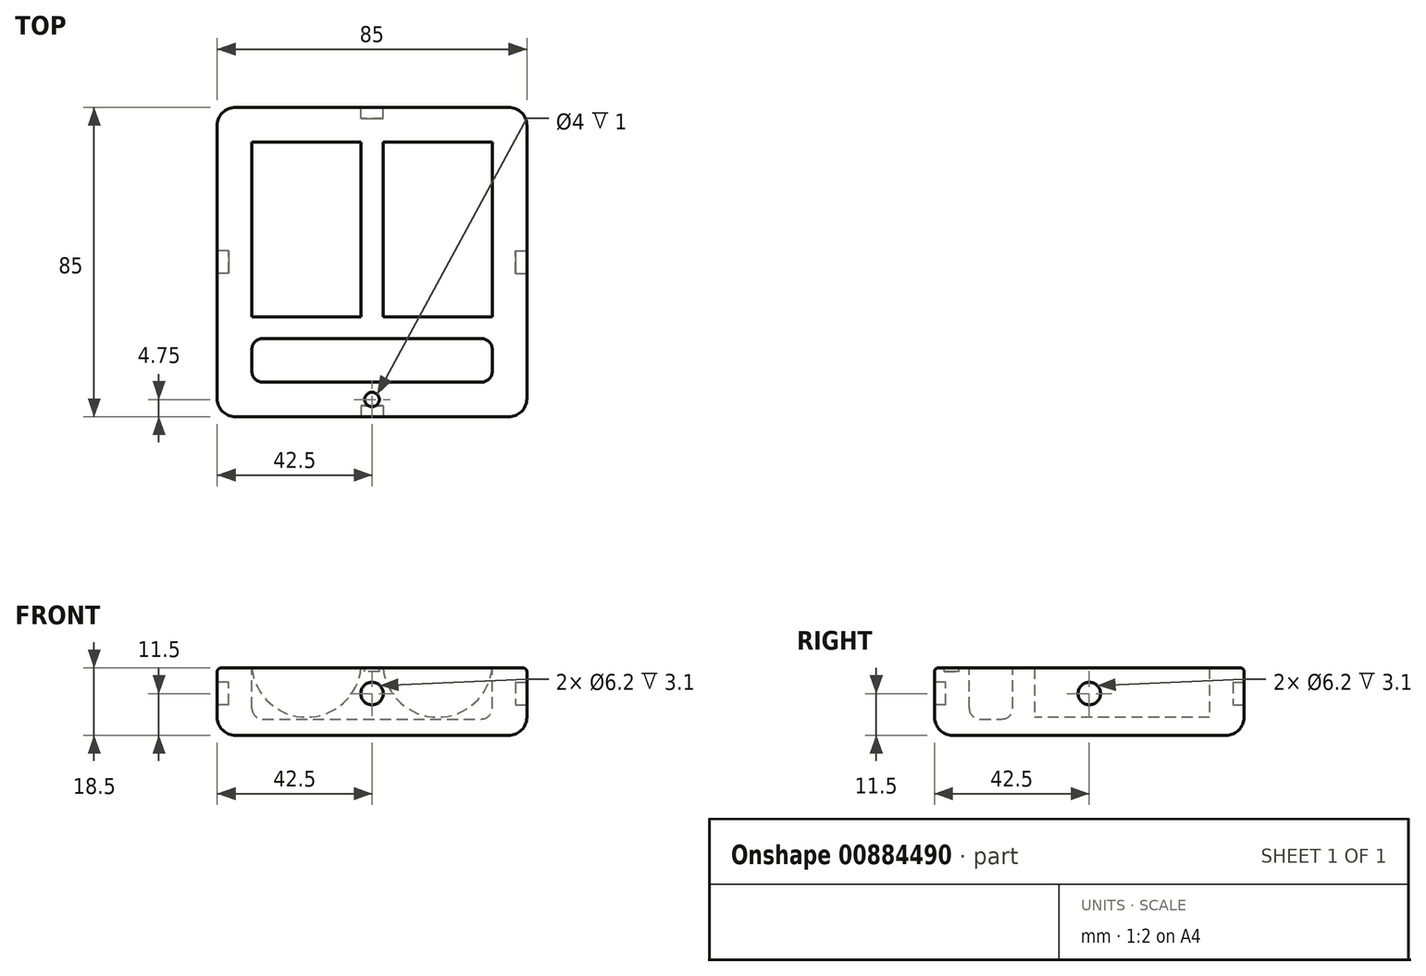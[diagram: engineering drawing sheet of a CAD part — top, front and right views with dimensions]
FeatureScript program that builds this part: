
annotation { "Feature Type Name" : "Feature", "Feature Type Description" : "" }
export const myFeature = defineFeature(function(context is Context, id is Id, definition is map)
    precondition{}
    {
        {
            var Q0;
            Q0=qCreatedBy(makeId("Top.planeOp"),FACE);
            var sketch = newSketch(context, id + "F0", { "sketchPlane" : qUnion([Q0])});
            skLineSegment(sketch, "E0.bottom", {"start": v(-42.5, 42.5) * mm, "end": v(42.5, 42.5) * mm});
            skLineSegment(sketch, "E0.top", {"start": v(-42.5, -42.5) * mm, "end": v(42.5, -42.5) * mm});
            skLineSegment(sketch, "E0.left", {"start": v(-42.5, 42.5) * mm, "end": v(-42.5, -42.5) * mm});
            skLineSegment(sketch, "E0.right", {"start": v(42.5, 42.5) * mm, "end": v(42.5, -42.5) * mm});
            skLineSegment(sketch, "E1.bottom", {"start": v(-30, 33) * mm, "end": v(30, 33) * mm});
            skLineSegment(sketch, "E1.top", {"start": v(-30, 21) * mm, "end": v(30, 21) * mm});
            skLineSegment(sketch, "E1.left", {"start": v(-33, 30) * mm, "end": v(-33, 24) * mm});
            skLineSegment(sketch, "E1.right", {"start": v(33, 30) * mm, "end": v(33, 24) * mm});
            skLineSegment(sketch, "E2.direction1", {"start": v(-33, 21) * mm, "end": v(-8.24, 21) * mm, "construction": true});
            skPoint(sketch, "E3.visualSharp", {"position": v(-33, 33) * mm});
            skArc(sketch, "E3.filletArc", {"start": v(-30, 33) * mm, "mid": v(-32.12, 32.12) * mm, "end": v(-33, 30) * mm});
            skPoint(sketch, "E4.visualSharp", {"position": v(33, 33) * mm});
            skArc(sketch, "E4.filletArc", {"start": v(33, 30) * mm, "mid": v(32.12, 32.12) * mm, "end": v(30, 33) * mm});
            skPoint(sketch, "E5.visualSharp", {"position": v(33, 21) * mm});
            skArc(sketch, "E5.filletArc", {"start": v(30, 21) * mm, "mid": v(32.12, 21.88) * mm, "end": v(33, 24) * mm});
            skPoint(sketch, "E6.visualSharp", {"position": v(-33, 21) * mm});
            skArc(sketch, "E6.filletArc", {"start": v(-33, 24) * mm, "mid": v(-32.12, 21.88) * mm, "end": v(-30, 21) * mm});
            skLineSegment(sketch, "E7.direction1", {"start": v(-33, 21) * mm, "end": v(-6.5, 21) * mm, "construction": true});
            skLineSegment(sketch, "E8", {"start": v(-42.5, 0) * mm, "end": v(42.5, 0) * mm, "construction": true});
            skLineSegment(sketch, "E9", {"start": v(0, -42.5) * mm, "end": v(0, 42.5) * mm, "construction": true});
            skCircle(sketch, "E10", {"center": v(0, 37.75) * mm, "radius": 2 * mm});
            skSolve(sketch);
        }
        {
            assignVariable(context, id + "F1", {"name" : "h", "anyValue" : 18.5});
        }
        {
            assignVariable(context, id + "F2", {"name" : "d", "anyValue" : 14});
        }
        {
            var Q0;
            Q0=makeQuery(id+"F0.imprint","IMPRINT",FACE,{"disambiguationData":[TD([[makeQuery(id+"F0.imprint","IMPRINT",EDGE,{"derivedFrom":sQuery(id+"F0.wireOp",EDGE,"E1.bottom")}),-1.0]])]});
            var Q1;
            Q1=makeQuery(id+"F0.imprint","IMPRINT",FACE,{"disambiguationData":[TD([[makeQuery(id+"F0.imprint","IMPRINT",EDGE,{"derivedFrom":sQuery(id+"F0.wireOp",EDGE,"E0.bottom")}),-1.0]])]});
            var Q2;
            Q2=makeQuery(id+"F0.imprint","IMPRINT",FACE,{"disambiguationData":[TD([[makeQuery(id+"F0.imprint","IMPRINT",EDGE,{"derivedFrom":sQuery(id+"F0.wireOp",EDGE,"E2.0.2.0")}),1.0]])]});
            var Q3;
            Q3=makeQuery(id+"F0.imprint","IMPRINT",FACE,{"disambiguationData":[TD([[makeQuery(id+"F0.imprint","IMPRINT",EDGE,{"derivedFrom":sQuery(id+"F0.wireOp",EDGE,"E2.0.3.0")}),1.0]])]});
            var Q4;
            Q4=makeQuery(id+"F0.imprint","IMPRINT",FACE,{"disambiguationData":[TD([[makeQuery(id+"F0.imprint","IMPRINT",EDGE,{"derivedFrom":sQuery(id+"F0.wireOp",EDGE,"E2.0.1.0")}),1.0]])]});
            var Q5;
            Q5=makeQuery(id+"F0.imprint","IMPRINT",FACE,{"disambiguationData":[TD([[makeQuery(id+"F0.imprint","IMPRINT",EDGE,{"derivedFrom":sQuery(id+"F0.wireOp",EDGE,"E7.0.1.2")}),1.0]])]});
            var Q6;
            Q6=makeQuery(id+"F0.imprint","IMPRINT",FACE,{"disambiguationData":[TD([[makeQuery(id+"F0.imprint","IMPRINT",EDGE,{"derivedFrom":sQuery(id+"F0.wireOp",EDGE,"E7.0.2.2")}),1.0]])]});
            var Q7;
            Q7=makeQuery(id+"F0.imprint","IMPRINT",FACE,{"disambiguationData":[TD([[makeQuery(id+"F0.imprint","IMPRINT",EDGE,{"derivedFrom":sQuery(id+"F0.wireOp",EDGE,"E7.0.3.2")}),1.0]])]});
            var Q8;
            Q8=makeQuery(id+"F0.imprint","IMPRINT",FACE,{"disambiguationData":[TD([[makeQuery(id+"F0.imprint","IMPRINT",EDGE,{"derivedFrom":sQuery(id+"F0.wireOp",EDGE,"46291ff4-7ef9-4f3a-836c-92f4481a90b5.bottom")}),-1.0]])]});
            var Q9;
            Q9=makeQuery(id+"F0.imprint","IMPRINT",FACE,{"disambiguationData":[TD([[makeQuery(id+"F0.imprint","IMPRINT",EDGE,{"derivedFrom":sQuery(id+"F0.wireOp",EDGE,"E10")}),1.0]])]});
            extrude(context, id + "F3", {"entities" : qUnion([Q0, Q1, Q2, Q3, Q4, Q5, Q6, Q7, Q8, Q9]), "depth" : (getVariable(context, 'h')) * mm, "offsetDistance" : 25 * mm});
        }
        {
            var Q0;
            Q0=makeQuery(id+"F0.imprint","IMPRINT",FACE,{"disambiguationData":[TD([[makeQuery(id+"F0.imprint","IMPRINT",EDGE,{"derivedFrom":sQuery(id+"F0.wireOp",EDGE,"E1.bottom")}),-1.0]])]});
            var Q1;
            Q1=makeQuery(id+"F0.imprint","IMPRINT",FACE,{"disambiguationData":[TD([[makeQuery(id+"F0.imprint","IMPRINT",EDGE,{"derivedFrom":sQuery(id+"F0.wireOp",EDGE,"E2.0.1.0")}),1.0]])]});
            var Q2;
            Q2=makeQuery(id+"F0.imprint","IMPRINT",FACE,{"disambiguationData":[TD([[makeQuery(id+"F0.imprint","IMPRINT",EDGE,{"derivedFrom":sQuery(id+"F0.wireOp",EDGE,"E2.0.2.0")}),1.0]])]});
            var Q3;
            Q3=makeQuery(id+"F0.imprint","IMPRINT",FACE,{"disambiguationData":[TD([[makeQuery(id+"F0.imprint","IMPRINT",EDGE,{"derivedFrom":sQuery(id+"F0.wireOp",EDGE,"E2.0.3.0")}),1.0]])]});
            var Q4;
            Q4=makeQuery(id+"F0.imprint","IMPRINT",FACE,{"disambiguationData":[TD([[makeQuery(id+"F0.imprint","IMPRINT",EDGE,{"derivedFrom":sQuery(id+"F0.wireOp",EDGE,"E7.0.1.2")}),1.0]])]});
            var Q5;
            Q5=makeQuery(id+"F0.imprint","IMPRINT",FACE,{"disambiguationData":[TD([[makeQuery(id+"F0.imprint","IMPRINT",EDGE,{"derivedFrom":sQuery(id+"F0.wireOp",EDGE,"E7.0.2.2")}),1.0]])]});
            var Q6;
            Q6=makeQuery(id+"F0.imprint","IMPRINT",FACE,{"disambiguationData":[TD([[makeQuery(id+"F0.imprint","IMPRINT",EDGE,{"derivedFrom":sQuery(id+"F0.wireOp",EDGE,"E7.0.3.2")}),1.0]])]});
            var Q7;
            Q7=makeQuery(id+"F0.imprint","IMPRINT",FACE,{"disambiguationData":[TD([[makeQuery(id+"F0.imprint","IMPRINT",EDGE,{"derivedFrom":sQuery(id+"F0.wireOp",EDGE,"46291ff4-7ef9-4f3a-836c-92f4481a90b5.bottom")}),-1.0]])]});
            extrude(context, id + "F4", {"entities" : qUnion([Q0, Q1, Q2, Q3, Q4, Q5, Q6, Q7]), "operationType" : NewBodyOperationType.REMOVE, "depth" : (getVariable(context, 'd')) * mm, "offsetDistance" : 25 * mm});
        }
        {
            var Q0;
            Q0=makeQuery(id+"F3.opExtrude","CAP_FACE",FACE,{"disambiguationData":[OSD([sQuery(id+"F0.wireOp",EDGE,"E0.bottom"),sQuery(id+"F0.wireOp",EDGE,"E0.top"),sQuery(id+"F0.wireOp",EDGE,"E0.left"),sQuery(id+"F0.wireOp",EDGE,"E0.right")])],"isStart":false});
            var Q1;
            Q1=makeQuery(id+"F3.opExtrude","SWEPT_EDGE",EDGE,{"disambiguationData":[OSD([sQuery(id+"F0.wireOp",EDGE,"E0.bottom"),sQuery(id+"F0.wireOp",EDGE,"E0.right")])]});
            var Q2;
            Q2=makeQuery(id+"F3.opExtrude","SWEPT_EDGE",EDGE,{"disambiguationData":[OSD([sQuery(id+"F0.wireOp",EDGE,"E0.bottom"),sQuery(id+"F0.wireOp",EDGE,"E0.left")])]});
            var Q3;
            Q3=makeQuery(id+"F3.opExtrude","SWEPT_EDGE",EDGE,{"disambiguationData":[OSD([sQuery(id+"F0.wireOp",EDGE,"E0.top"),sQuery(id+"F0.wireOp",EDGE,"E0.left")])]});
            var Q4;
            Q4=makeQuery(id+"F3.opExtrude","SWEPT_EDGE",EDGE,{"disambiguationData":[OSD([sQuery(id+"F0.wireOp",EDGE,"E0.top"),sQuery(id+"F0.wireOp",EDGE,"E0.right")])]});
            fillet(context, id + "F5", {"entities" : qUnion([Q0, Q1, Q2, Q3, Q4]), "radius" : 5 * mm, "tangentPropagation" : true, "allowEdgeOverflow" : false});
        }
        {
            var Q0;
            Q0=makeQuery(id+"F4.boolean.opBoolean","COPY",FACE,{"derivedFrom":makeQuery(id+"F4.opExtrude","CAP_FACE",FACE,{"disambiguationData":[OSD([sQuery(id+"F0.wireOp",EDGE,"E1.bottom"),sQuery(id+"F0.wireOp",EDGE,"E1.top"),sQuery(id+"F0.wireOp",EDGE,"E1.left"),sQuery(id+"F0.wireOp",EDGE,"E1.right"),sQuery(id+"F0.wireOp",EDGE,"E3.filletArc"),sQuery(id+"F0.wireOp",EDGE,"E4.filletArc"),sQuery(id+"F0.wireOp",EDGE,"E5.filletArc"),sQuery(id+"F0.wireOp",EDGE,"E6.filletArc")])],"isStart":false})});
            var Q1;
            Q1=makeQuery(id+"F4.boolean.opBoolean","COPY",FACE,{"derivedFrom":makeQuery(id+"F4.opExtrude","CAP_FACE",FACE,{"disambiguationData":[OSD([sQuery(id+"F0.wireOp",EDGE,"E7.0.1.2"),sQuery(id+"F0.wireOp",EDGE,"E7.0.1.4"),sQuery(id+"F0.wireOp",EDGE,"E7.0.1.5"),sQuery(id+"F0.wireOp",EDGE,"E7.0.1.6"),sQuery(id+"F0.wireOp",EDGE,"E7.0.1.7"),sQuery(id+"F0.wireOp",EDGE,"E7.0.1.9"),sQuery(id+"F0.wireOp",EDGE,"E7.0.1.11"),sQuery(id+"F0.wireOp",EDGE,"E7.0.1.12")])],"isStart":false})});
            var Q2;
            Q2=makeQuery(id+"F4.boolean.opBoolean","COPY",FACE,{"derivedFrom":makeQuery(id+"F4.opExtrude","CAP_FACE",FACE,{"disambiguationData":[OSD([sQuery(id+"F0.wireOp",EDGE,"E7.0.2.2"),sQuery(id+"F0.wireOp",EDGE,"E7.0.2.4"),sQuery(id+"F0.wireOp",EDGE,"E7.0.2.5"),sQuery(id+"F0.wireOp",EDGE,"E7.0.2.6"),sQuery(id+"F0.wireOp",EDGE,"E7.0.2.7"),sQuery(id+"F0.wireOp",EDGE,"E7.0.2.9"),sQuery(id+"F0.wireOp",EDGE,"E7.0.2.11"),sQuery(id+"F0.wireOp",EDGE,"E7.0.2.12")])],"isStart":false})});
            var Q3;
            Q3=makeQuery(id+"F4.boolean.opBoolean","COPY",FACE,{"derivedFrom":makeQuery(id+"F4.opExtrude","CAP_FACE",FACE,{"disambiguationData":[OSD([sQuery(id+"F0.wireOp",EDGE,"E7.0.3.2"),sQuery(id+"F0.wireOp",EDGE,"E7.0.3.4"),sQuery(id+"F0.wireOp",EDGE,"E7.0.3.5"),sQuery(id+"F0.wireOp",EDGE,"E7.0.3.6"),sQuery(id+"F0.wireOp",EDGE,"E7.0.3.7"),sQuery(id+"F0.wireOp",EDGE,"E7.0.3.9"),sQuery(id+"F0.wireOp",EDGE,"E7.0.3.11"),sQuery(id+"F0.wireOp",EDGE,"E7.0.3.12")])],"isStart":false})});
            var Q4;
            Q4=makeQuery(id+"F4.boolean.opBoolean","COPY",FACE,{"derivedFrom":makeQuery(id+"F4.opExtrude","CAP_FACE",FACE,{"disambiguationData":[OSD([sQuery(id+"F0.wireOp",EDGE,"46291ff4-7ef9-4f3a-836c-92f4481a90b5.bottom"),sQuery(id+"F0.wireOp",EDGE,"46291ff4-7ef9-4f3a-836c-92f4481a90b5.top"),sQuery(id+"F0.wireOp",EDGE,"46291ff4-7ef9-4f3a-836c-92f4481a90b5.left"),sQuery(id+"F0.wireOp",EDGE,"46291ff4-7ef9-4f3a-836c-92f4481a90b5.right"),sQuery(id+"F0.wireOp",EDGE,"f9652c3b-33d4-4875-8296-8c731cea0ff2.filletArc"),sQuery(id+"F0.wireOp",EDGE,"bc3a633f-a680-41aa-ad19-7ac7e5a684a1.filletArc"),sQuery(id+"F0.wireOp",EDGE,"cd018c40-e85b-49f8-971f-61b861827422.filletArc"),sQuery(id+"F0.wireOp",EDGE,"71912b40-0116-4324-a46e-baf74d7a231e.filletArc")])],"isStart":false})});
            fillet(context, id + "F6", {"entities" : qUnion([Q0, Q1, Q2, Q3, Q4]), "radius" : 3 * mm, "tangentPropagation" : true, "allowEdgeOverflow" : false});
        }
        {
            var Q0;
            Q0=makeQuery(id+"F3.opExtrude","SWEPT_FACE",FACE,{"disambiguationData":[OSD([sQuery(id+"F0.wireOp",EDGE,"E0.top")])]});
            var sketch = newSketch(context, id + "F7", { "sketchPlane" : qUnion([Q0])});
            skCircle(sketch, "E11", {"center": v(0, 7) * mm, "radius": 3.1 * mm});
            skSolve(sketch);
        }
        {
            var Q0;
            Q0=makeQuery(id+"F7.imprint","IMPRINT",FACE,{"disambiguationData":[TD([[makeQuery(id+"F7.imprint","IMPRINT",EDGE,{"derivedFrom":sQuery(id+"F7.wireOp",EDGE,"E11")}),1.0]])]});
            extrude(context, id + "F8", {"entities" : qUnion([Q0]), "operationType" : NewBodyOperationType.REMOVE, "oppositeDirection" : true, "depth" : 3.1 * mm, "offsetDistance" : 25 * mm});
        }
        {
            var Q0;
            Q0=makeQuery(id+"F3.opExtrude","SWEPT_FACE",FACE,{"disambiguationData":[OSD([sQuery(id+"F0.wireOp",EDGE,"E0.bottom")])]});
            var sketch = newSketch(context, id + "F9", { "sketchPlane" : qUnion([Q0])});
            skCircle(sketch, "E12", {"center": v(0, 7) * mm, "radius": 3.1 * mm});
            skSolve(sketch);
        }
        {
            var Q0;
            Q0=makeQuery(id+"F9.imprint","IMPRINT",FACE,{"disambiguationData":[TD([[makeQuery(id+"F9.imprint","IMPRINT",EDGE,{"derivedFrom":sQuery(id+"F9.wireOp",EDGE,"E12")}),1.0]])]});
            extrude(context, id + "F10", {"entities" : qUnion([Q0]), "operationType" : NewBodyOperationType.REMOVE, "oppositeDirection" : true, "depth" : 3.1 * mm, "offsetDistance" : 25 * mm});
        }
        {
            var Q0;
            Q0=makeQuery(id+"F3.opExtrude","SWEPT_FACE",FACE,{"disambiguationData":[OSD([sQuery(id+"F0.wireOp",EDGE,"E0.left")])]});
            var sketch = newSketch(context, id + "F11", { "sketchPlane" : qUnion([Q0])});
            skCircle(sketch, "E13", {"center": v(0, 7) * mm, "radius": 3.1 * mm});
            skSolve(sketch);
        }
        {
            var Q0;
            Q0=makeQuery(id+"F11.imprint","IMPRINT",FACE,{"disambiguationData":[TD([[makeQuery(id+"F11.imprint","IMPRINT",EDGE,{"derivedFrom":sQuery(id+"F11.wireOp",EDGE,"E13")}),1.0]])]});
            extrude(context, id + "F12", {"entities" : qUnion([Q0]), "operationType" : NewBodyOperationType.REMOVE, "oppositeDirection" : true, "depth" : 3.1 * mm, "offsetDistance" : 25 * mm});
        }
        {
            var Q0;
            Q0=makeQuery(id+"F3.opExtrude","SWEPT_FACE",FACE,{"disambiguationData":[OSD([sQuery(id+"F0.wireOp",EDGE,"E0.right")])]});
            var sketch = newSketch(context, id + "F13", { "sketchPlane" : qUnion([Q0])});
            skCircle(sketch, "E14", {"center": v(0, 7) * mm, "radius": 3.1 * mm});
            skSolve(sketch);
        }
        {
            var Q0;
            Q0=makeQuery(id+"F13.imprint","IMPRINT",FACE,{"disambiguationData":[TD([[makeQuery(id+"F13.imprint","IMPRINT",EDGE,{"derivedFrom":sQuery(id+"F13.wireOp",EDGE,"E14")}),1.0]])]});
            extrude(context, id + "F14", {"entities" : qUnion([Q0]), "operationType" : NewBodyOperationType.REMOVE, "oppositeDirection" : true, "depth" : 3.1 * mm, "offsetDistance" : 25 * mm});
        }
        {
            var Q0;
            Q0=makeQuery(id+"F0.imprint","IMPRINT",FACE,{"disambiguationData":[TD([[makeQuery(id+"F0.imprint","IMPRINT",EDGE,{"derivedFrom":sQuery(id+"F0.wireOp",EDGE,"E10")}),1.0]])]});
            extrude(context, id + "F15", {"entities" : qUnion([Q0]), "operationType" : NewBodyOperationType.REMOVE, "depth" : 1 * mm, "offsetDistance" : 25 * mm});
        }
        {
            var Q0;
            Q0=makeQuery(id+"F3.opExtrude","SWEPT_FACE",FACE,{"disambiguationData":[OSD([sQuery(id+"F0.wireOp",EDGE,"E0.bottom")])]});
            cPlane(context, id + "F16", {"entities" : qUnion([Q0]), "cplaneType" : CPlaneType.OFFSET, "offset" : 27.5 * mm, "oppositeDirection" : true, "width" : 150 * mm, "height" : 150 * mm});
        }
        {
            var Q0;
            Q0=qCreatedBy(id+"F16.planeOp",FACE);
            var sketch = newSketch(context, id + "F17", { "sketchPlane" : qUnion([Q0])});
            skArc(sketch, "E15", {"start": v(-3, 0) * mm, "mid": v(-18, 13.5) * mm, "end": v(-33, 0) * mm});
            skLineSegment(sketch, "E16", {"start": v(-3, 0) * mm, "end": v(-3, 13.5) * mm, "construction": true});
            skLineSegment(sketch, "E17", {"start": v(-33, 13.5) * mm, "end": v(-33, 0) * mm, "construction": true});
            skLineSegment(sketch, "E18", {"start": v(-33, 13.5) * mm, "end": v(-3, 13.5) * mm, "construction": true});
            skPoint(sketch, "E18.endSnap0", {"position": v(-3, 16.26) * mm});
            skLineSegment(sketch, "E19.trimOffspring", {"start": v(-3, 16.26) * mm, "end": v(-3, 35.2) * mm, "construction": true});
            skLineSegment(sketch, "E20", {"start": v(-33, 0) * mm, "end": v(-3, 0) * mm});
            skPoint(sketch, "E21.orphan", {"position": v(-47.15, 0) * mm});
            skPoint(sketch, "E22.orphan", {"position": v(-3, -2.69) * mm});
            skLineSegment(sketch, "E23.MirrorCS", {"start": v(33, 0) * mm, "end": v(3, 0) * mm});
            skArc(sketch, "E24.MirrorCS", {"start": v(3, 0) * mm, "mid": v(18, 13.5) * mm, "end": v(33, 0) * mm});
            skSolve(sketch);
        }
        {
            var Q0;
            Q0=makeQuery(id+"F17.imprint","IMPRINT",FACE,{"disambiguationData":[TD([[makeQuery(id+"F17.imprint","IMPRINT",EDGE,{"derivedFrom":sQuery(id+"F17.wireOp",EDGE,"E15")}),1.0]])]});
            var Q1;
            Q1=makeQuery(id+"F17.imprint","IMPRINT",FACE,{"disambiguationData":[TD([[makeQuery(id+"F17.imprint","IMPRINT",EDGE,{"derivedFrom":sQuery(id+"F17.wireOp",EDGE,"E23.MirrorCS")}),-1.0]])]});
            extrude(context, id + "F18", {"entities" : qUnion([Q0, Q1]), "operationType" : NewBodyOperationType.REMOVE, "oppositeDirection" : true, "depth" : 48 * mm, "offsetDistance" : 25 * mm});
        }
        {
            var Q0;
            Q0=makeQuery(id+"F3.opExtrude","CAP_EDGE",EDGE,{"disambiguationData":[OSD([sQuery(id+"F0.wireOp",EDGE,"E0.left")])],"isStart":true});
            var Q1;
            {var subQ0=sQuery(id+"F17.wireOp",EDGE,"E24.MirrorCS");var subQ1=sQuery(id+"F17.wireOp",EDGE,"E23.MirrorCS");Q1=makeQuery(id+"F18.boolean.opBoolean","COPY",EDGE,{"derivedFrom":makeQuery(id+"F18.opExtrude","SWEPT_EDGE",EDGE,{"disambiguationData":[OSD([subQ1,subQ0]),TDD([makeQuery(id+"F17.imprint","INTERSECT",VERTEX,{"disambiguationData":[OD(0.0)],"derivedFrom":[subQ1,subQ0]})])]})});}
            var Q2;
            Q2=makeQuery(id+"F18.boolean.opBoolean","COPY",EDGE,{"derivedFrom":makeQuery(id+"F18.opExtrude","CAP_EDGE",EDGE,{"disambiguationData":[OSD([sQuery(id+"F17.wireOp",EDGE,"E23.MirrorCS")])],"isStart":true})});
            var Q3;
            {var subQ0=sQuery(id+"F17.wireOp",EDGE,"E24.MirrorCS");var subQ1=sQuery(id+"F17.wireOp",EDGE,"E23.MirrorCS");Q3=makeQuery(id+"F18.boolean.opBoolean","COPY",EDGE,{"derivedFrom":makeQuery(id+"F18.opExtrude","SWEPT_EDGE",EDGE,{"disambiguationData":[OSD([subQ1,subQ0]),TDD([makeQuery(id+"F17.imprint","INTERSECT",VERTEX,{"disambiguationData":[OD(1.0)],"derivedFrom":[subQ1,subQ0]})])]})});}
            var Q4;
            Q4=makeQuery(id+"F18.boolean.opBoolean","COPY",EDGE,{"derivedFrom":makeQuery(id+"F18.opExtrude","CAP_EDGE",EDGE,{"disambiguationData":[OSD([sQuery(id+"F17.wireOp",EDGE,"E23.MirrorCS")])],"isStart":false})});
            var Q5;
            {var subQ0=sQuery(id+"F17.wireOp",EDGE,"E20");var subQ1=sQuery(id+"F17.wireOp",EDGE,"E15");Q5=makeQuery(id+"F18.boolean.opBoolean","COPY",EDGE,{"derivedFrom":makeQuery(id+"F18.opExtrude","SWEPT_EDGE",EDGE,{"disambiguationData":[OSD([subQ1,subQ0]),TDD([makeQuery(id+"F17.imprint","INTERSECT",VERTEX,{"disambiguationData":[OD(0.0)],"derivedFrom":[subQ1,subQ0]})])]})});}
            var Q6;
            Q6=makeQuery(id+"F18.boolean.opBoolean","COPY",EDGE,{"derivedFrom":makeQuery(id+"F18.opExtrude","CAP_EDGE",EDGE,{"disambiguationData":[OSD([sQuery(id+"F17.wireOp",EDGE,"E20")])],"isStart":false})});
            var Q7;
            {var subQ0=sQuery(id+"F17.wireOp",EDGE,"E20");var subQ1=sQuery(id+"F17.wireOp",EDGE,"E15");Q7=makeQuery(id+"F18.boolean.opBoolean","COPY",EDGE,{"derivedFrom":makeQuery(id+"F18.opExtrude","SWEPT_EDGE",EDGE,{"disambiguationData":[OSD([subQ1,subQ0]),TDD([makeQuery(id+"F17.imprint","INTERSECT",VERTEX,{"disambiguationData":[OD(1.0)],"derivedFrom":[subQ1,subQ0]})])]})});}
            var Q8;
            Q8=makeQuery(id+"F18.boolean.opBoolean","COPY",EDGE,{"derivedFrom":makeQuery(id+"F18.opExtrude","CAP_EDGE",EDGE,{"disambiguationData":[OSD([sQuery(id+"F17.wireOp",EDGE,"E20")])],"isStart":true})});
            var Q9;
            Q9=makeQuery(id+"F4.boolean.opBoolean","COPY",EDGE,{"derivedFrom":makeQuery(id+"F4.opExtrude","CAP_EDGE",EDGE,{"disambiguationData":[OSD([sQuery(id+"F0.wireOp",EDGE,"E1.top")])],"isStart":true})});
            fillet(context, id + "F19", {"entities" : qUnion([Q0, Q1, Q2, Q3, Q4, Q5, Q6, Q7, Q8, Q9]), "radius" : 1 * mm, "tangentPropagation" : true, "allowEdgeOverflow" : false});
        }
        {
            var Q0;
            Q0=makeQuery(id+"F3.opExtrude","SWEPT_BODY",BODY,{"disambiguationData":[OSD([sQuery(id+"F0.wireOp",EDGE,"E0.bottom"),sQuery(id+"F0.wireOp",EDGE,"E0.top"),sQuery(id+"F0.wireOp",EDGE,"E0.left"),sQuery(id+"F0.wireOp",EDGE,"E0.right")])]});
            var Q1;
            Q1=sQuery(id+"F0.wireOp",EDGE,"E8");
            transform(context, id + "F20", {"entities" : qUnion([Q0]), "transformType" : TransformType.ROTATION, "transformAxis" : qUnion([Q1]), "angle" : 180 * degree, "makeCopy" : false});
        }
    });
